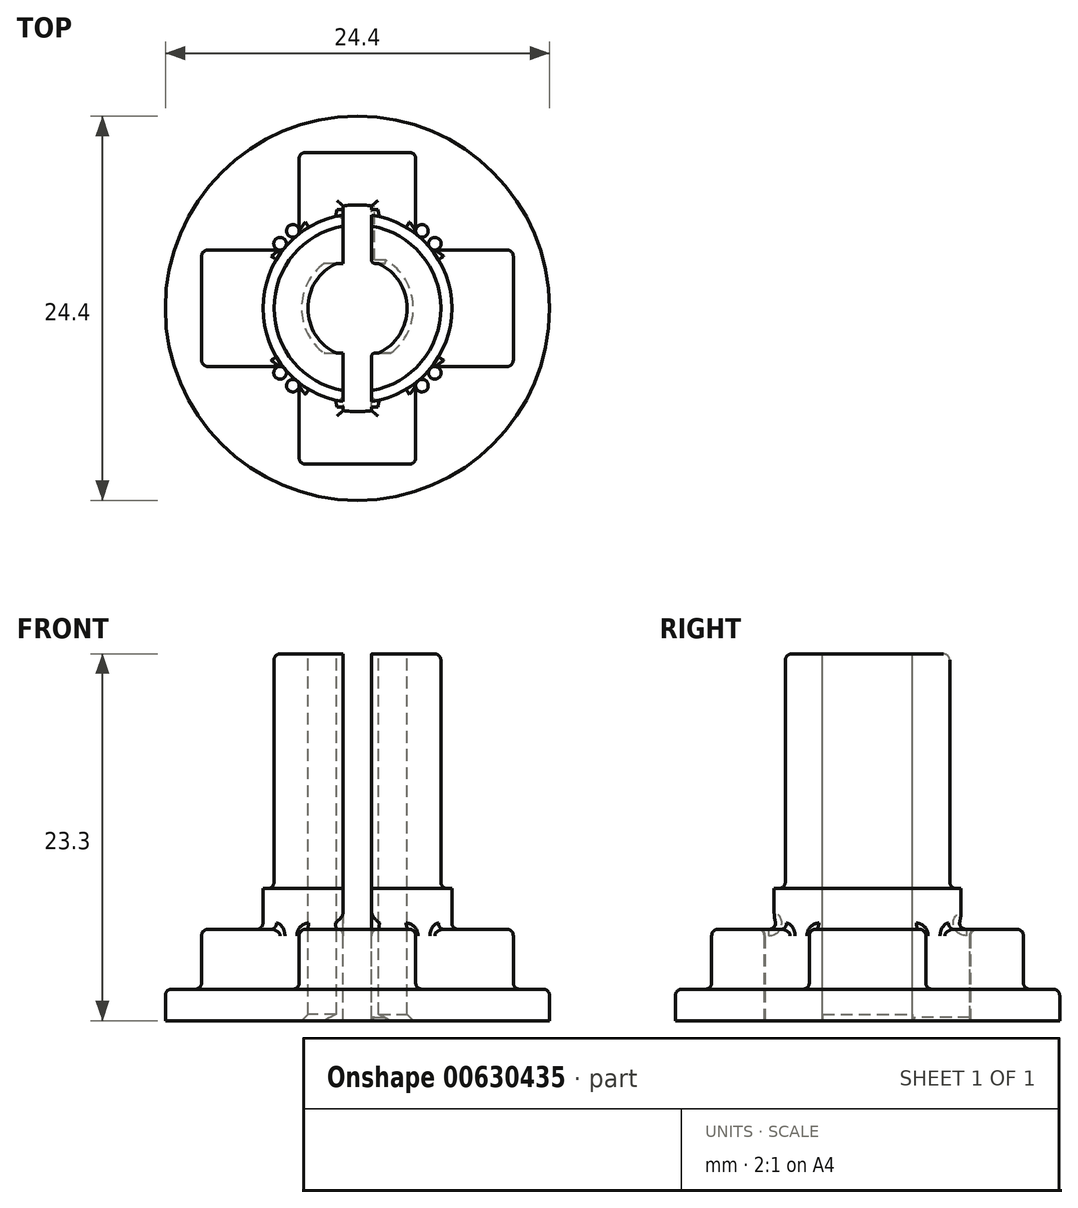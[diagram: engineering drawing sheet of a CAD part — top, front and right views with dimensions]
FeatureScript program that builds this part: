
annotation { "Feature Type Name" : "Feature", "Feature Type Description" : "" }
export const myFeature = defineFeature(function(context is Context, id is Id, definition is map)
    precondition{}
    {
        {
            var Q0;
            Q0=qCreatedBy(makeId("Front.planeOp"),FACE);
            var sketch = newSketch(context, id + "F0", { "sketchPlane" : qUnion([Q0])});
            skLineSegment(sketch, "E0", {"start": v(-12.2, 2) * mm, "end": v(-12.2, 0) * mm});
            skLineSegment(sketch, "E1", {"start": v(-12.2, 2) * mm, "end": v(-6, 2) * mm});
            skLineSegment(sketch, "E2", {"start": v(-6, 2) * mm, "end": v(-6, 8.4) * mm});
            skLineSegment(sketch, "E3", {"start": v(-6, 8.4) * mm, "end": v(-5.3, 8.4) * mm});
            skLineSegment(sketch, "E4", {"start": v(-5.3, 8.4) * mm, "end": v(-5.3, 23.3) * mm});
            skLineSegment(sketch, "E5", {"start": v(0, 23.3) * mm, "end": v(0, 0) * mm});
            skLineSegment(sketch, "E6", {"start": v(-5.3, 23.3) * mm, "end": v(-3.15, 23.3) * mm});
            skLineSegment(sketch, "E7", {"start": v(-3.15, 23.3) * mm, "end": v(-3.15, 0) * mm});
            skLineSegment(sketch, "E8", {"start": v(-12.2, 0) * mm, "end": v(-3.15, 0) * mm});
            skSolve(sketch);
        }
        {
            var Q0;
            Q0=makeQuery(id+"F0.imprint","IMPRINT",FACE,{"disambiguationData":[TD([[makeQuery(id+"F0.imprint","IMPRINT",EDGE,{"derivedFrom":sQuery(id+"F0.wireOp",EDGE,"E0")}),1.0]])]});
            var Q1;
            Q1=sQuery(id+"F0.wireOp",EDGE,"E5");
            revolve(context, id + "F1", {"entities" : qUnion([Q0]), "axis" : qUnion([Q1]), "revolveType" : RevolveType.FULL});
        }
        {
            var Q0;
            Q0=makeQuery(id+"F1.opRevolve","SWEPT_FACE",FACE,{"disambiguationData":[OSD([sQuery(id+"F0.wireOp",EDGE,"E1")])]});
            var sketch = newSketch(context, id + "F2", { "sketchPlane" : qUnion([Q0])});
            skCircle(sketch, "E9.0", {"center": v(0, 0) * mm, "radius": 6 * mm});
            skLineSegment(sketch, "E10", {"start": v(-3.7, 9.9) * mm, "end": v(3.7, 9.9) * mm});
            skLineSegment(sketch, "E11", {"start": v(3.7, 9.9) * mm, "end": v(3.7, 4.72) * mm});
            skLineSegment(sketch, "E12", {"start": v(-3.7, 9.9) * mm, "end": v(-3.7, 4.72) * mm});
            skLineSegment(sketch, "E13.1.0", {"start": v(-9.9, -3.7) * mm, "end": v(-4.72, -3.7) * mm});
            skLineSegment(sketch, "E13.1.1", {"start": v(-9.9, -3.7) * mm, "end": v(-9.9, 3.7) * mm});
            skLineSegment(sketch, "E13.1.2", {"start": v(-9.9, 3.7) * mm, "end": v(-4.72, 3.7) * mm});
            skLineSegment(sketch, "E13.2.0", {"start": v(3.7, -9.9) * mm, "end": v(3.7, -4.72) * mm});
            skLineSegment(sketch, "E13.2.1", {"start": v(3.7, -9.9) * mm, "end": v(-3.7, -9.9) * mm});
            skLineSegment(sketch, "E13.2.2", {"start": v(-3.7, -9.9) * mm, "end": v(-3.7, -4.72) * mm});
            skLineSegment(sketch, "E13.3.0", {"start": v(9.9, 3.7) * mm, "end": v(4.72, 3.7) * mm});
            skLineSegment(sketch, "E13.3.1", {"start": v(9.9, 3.7) * mm, "end": v(9.9, -3.7) * mm});
            skLineSegment(sketch, "E13.3.2", {"start": v(9.9, -3.7) * mm, "end": v(4.72, -3.7) * mm});
            skSolve(sketch);
        }
        {
            var Q0;
            {var subQ0=sQuery(id+"F2.wireOp",EDGE,"E13.1.0");Q0=makeQuery(id+"F2.imprint","IMPRINT",FACE,{"disambiguationData":[TD([[makeQuery(id+"F2.imprint","IMPRINT",EDGE,{"derivedFrom":subQ0}),1.0]])]});}
            var Q1;
            {var subQ0=sQuery(id+"F2.wireOp",EDGE,"E13.2.0");Q1=makeQuery(id+"F2.imprint","IMPRINT",FACE,{"disambiguationData":[TD([[makeQuery(id+"F2.imprint","IMPRINT",EDGE,{"derivedFrom":subQ0}),1.0]])]});}
            var Q2;
            {var subQ0=sQuery(id+"F2.wireOp",EDGE,"E13.3.0");Q2=makeQuery(id+"F2.imprint","IMPRINT",FACE,{"disambiguationData":[TD([[makeQuery(id+"F2.imprint","IMPRINT",EDGE,{"derivedFrom":subQ0}),1.0]])]});}
            var Q3;
            Q3=makeQuery(id+"F2.imprint","IMPRINT",FACE,{"disambiguationData":[TD([[makeQuery(id+"F2.imprint","IMPRINT",EDGE,{"derivedFrom":sQuery(id+"F2.wireOp",EDGE,"E10")}),-1.0]])]});
            extrude(context, id + "F3", {"entities" : qUnion([Q0, Q1, Q2, Q3]), "operationType" : NewBodyOperationType.ADD, "depth" : 3.8 * mm, "offsetDistance" : 25 * mm});
        }
        {
            var Q0;
            Q0=makeQuery(id+"F1.opRevolve","SWEPT_FACE",FACE,{"disambiguationData":[OSD([sQuery(id+"F0.wireOp",EDGE,"E6")])]});
            var sketch = newSketch(context, id + "F4", { "sketchPlane" : qUnion([Q0])});
            skCircle(sketch, "E14.0", {"center": v(0, 0) * mm, "radius": 3.15 * mm});
            skLineSegment(sketch, "E15", {"start": v(1.34, 2.85) * mm, "end": v(-1.34, 2.85) * mm});
            skLineSegment(sketch, "E16", {"start": v(1.34, -2.85) * mm, "end": v(-1.34, -2.85) * mm});
            skSolve(sketch);
        }
        {
            var Q0;
            {var subQ0=sQuery(id+"F4.wireOp",EDGE,"E15");Q0=makeQuery(id+"F4.imprint","IMPRINT",FACE,{"disambiguationData":[TD([[makeQuery(id+"F4.imprint","IMPRINT",EDGE,{"derivedFrom":subQ0}),-1.0]])]});}
            var Q1;
            {var subQ0=sQuery(id+"F4.wireOp",EDGE,"E16");Q1=makeQuery(id+"F4.imprint","IMPRINT",FACE,{"disambiguationData":[TD([[makeQuery(id+"F4.imprint","IMPRINT",EDGE,{"derivedFrom":subQ0}),1.0]])]});}
            var Q2;
            Q2=makeQuery(id+"F1.opRevolve","SWEPT_FACE",FACE,{"disambiguationData":[OSD([sQuery(id+"F0.wireOp",EDGE,"E8")])]});
            extrude(context, id + "F5", {"entities" : qUnion([Q0, Q1]), "operationType" : NewBodyOperationType.ADD, "endBound" : BoundingType.UP_TO_SURFACE, "oppositeDirection" : true, "depth" : 25 * mm, "endBoundEntityFace" : qUnion([Q2]), "offsetDistance" : 25 * mm});
        }
        {
            var Q0;
            {var subQ0=sQuery(id+"F4.wireOp",EDGE,"E14.0");Q0=makeQuery(id+"F5.boolean.opBoolean","MERGE",FACE,{"derivedFrom":[makeQuery(id+"F1.opRevolve","SWEPT_FACE",FACE,{"disambiguationData":[OSD([sQuery(id+"F0.wireOp",EDGE,"E6")])]}),makeQuery(id+"F5.opExtrude","CAP_FACE",FACE,{"disambiguationData":[OSD([subQ0,sQuery(id+"F4.wireOp",EDGE,"E15")])],"isStart":true}),makeQuery(id+"F5.opExtrude","CAP_FACE",FACE,{"disambiguationData":[OSD([subQ0,sQuery(id+"F4.wireOp",EDGE,"E16")])],"isStart":true})]});}
            var sketch = newSketch(context, id + "F6", { "sketchPlane" : qUnion([Q0])});
            skLineSegment(sketch, "E17", {"start": v(0.9, -2.85) * mm, "end": v(0.9, -6.5) * mm});
            skLineSegment(sketch, "E18", {"start": v(0.9, -6.5) * mm, "end": v(-0.9, -6.5) * mm});
            skLineSegment(sketch, "E19", {"start": v(-0.9, -6.5) * mm, "end": v(-0.9, -2.85) * mm});
            skLineSegment(sketch, "E20.1.0", {"start": v(-0.9, 2.85) * mm, "end": v(-0.9, 6.5) * mm});
            skLineSegment(sketch, "E20.1.1", {"start": v(-0.9, 6.5) * mm, "end": v(0.9, 6.5) * mm});
            skLineSegment(sketch, "E20.1.2", {"start": v(0.9, 6.5) * mm, "end": v(0.9, 2.85) * mm});
            skPoint(sketch, "E20.center", {"position": v(0, 0) * mm});
            skArc(sketch, "E21", {"start": v(0.9, 6.5) * mm, "mid": v(0, 6.56) * mm, "end": v(-0.9, 6.5) * mm});
            skArc(sketch, "E22.trimOffspring", {"start": v(-0.9, -6.5) * mm, "mid": v(0, -6.56) * mm, "end": v(0.9, -6.5) * mm});
            skSolve(sketch);
        }
        {
            var Q0;
            {var subQ0=sQuery(id+"F6.wireOp",EDGE,"E17");Q0=makeQuery(id+"F6.imprint","IMPRINT",FACE,{"disambiguationData":[TD([[makeQuery(id+"F6.imprint","IMPRINT",EDGE,{"derivedFrom":subQ0}),-1.0]])]});}
            var Q1;
            {var subQ0=sQuery(id+"F6.wireOp",EDGE,"E20.1.0");Q1=makeQuery(id+"F6.imprint","IMPRINT",FACE,{"disambiguationData":[TD([[makeQuery(id+"F6.imprint","IMPRINT",EDGE,{"derivedFrom":subQ0}),-1.0]])]});}
            var Q2;
            Q2=makeQuery(id+"F6.imprint","IMPRINT",FACE,{"disambiguationData":[TD([[makeQuery(id+"F6.imprint","IMPRINT",EDGE,{"derivedFrom":sQuery(id+"F6.wireOp",EDGE,"E18")}),1.0]])]});
            var Q3;
            Q3=makeQuery(id+"F6.imprint","IMPRINT",FACE,{"disambiguationData":[TD([[makeQuery(id+"F6.imprint","IMPRINT",EDGE,{"derivedFrom":sQuery(id+"F6.wireOp",EDGE,"E20.1.1")}),1.0]])]});
            var Q4;
            {var subQ0=sQuery(id+"F4.wireOp",EDGE,"E14.0");Q4=makeQuery(id+"F5.boolean.opBoolean","MERGE",FACE,{"derivedFrom":[makeQuery(id+"F1.opRevolve","SWEPT_FACE",FACE,{"disambiguationData":[OSD([sQuery(id+"F0.wireOp",EDGE,"E8")])]}),makeQuery(id+"F5.opExtrude","CAP_FACE",FACE,{"disambiguationData":[OSD([subQ0,sQuery(id+"F4.wireOp",EDGE,"E15")])],"isStart":false}),makeQuery(id+"F5.opExtrude","CAP_FACE",FACE,{"disambiguationData":[OSD([subQ0,sQuery(id+"F4.wireOp",EDGE,"E16")])],"isStart":false})]});}
            extrude(context, id + "F7", {"entities" : qUnion([Q0, Q1, Q2, Q3]), "operationType" : NewBodyOperationType.REMOVE, "endBound" : BoundingType.UP_TO_SURFACE, "oppositeDirection" : true, "depth" : 25 * mm, "endBoundEntityFace" : qUnion([Q4]), "offsetDistance" : 25 * mm});
        }
        {
            var Q0;
            Q0=makeQuery(id+"F1.opRevolve","SWEPT_FACE",FACE,{"disambiguationData":[OSD([sQuery(id+"F0.wireOp",EDGE,"E1")])]});
            var Q1;
            Q1=makeQuery(id+"F3.opExtrude","SWEPT_FACE",FACE,{"disambiguationData":[OSD([sQuery(id+"F2.wireOp",EDGE,"E13.3.0")])]});
            var Q2;
            Q2=makeQuery(id+"F3.opExtrude","CAP_FACE",FACE,{"disambiguationData":[OSD([sQuery(id+"F2.wireOp",EDGE,"E9.0"),sQuery(id+"F2.wireOp",EDGE,"E13.3.0"),sQuery(id+"F2.wireOp",EDGE,"E13.3.1"),sQuery(id+"F2.wireOp",EDGE,"E13.3.2")])],"isStart":false});
            var Q3;
            Q3=makeQuery(id+"F3.opExtrude","SWEPT_FACE",FACE,{"disambiguationData":[OSD([sQuery(id+"F2.wireOp",EDGE,"E13.3.2")])]});
            var Q4;
            Q4=makeQuery(id+"F3.opExtrude","SWEPT_FACE",FACE,{"disambiguationData":[OSD([sQuery(id+"F2.wireOp",EDGE,"E11")])]});
            var Q5;
            Q5=makeQuery(id+"F3.opExtrude","CAP_FACE",FACE,{"disambiguationData":[OSD([sQuery(id+"F2.wireOp",EDGE,"E9.0"),sQuery(id+"F2.wireOp",EDGE,"E10"),sQuery(id+"F2.wireOp",EDGE,"E11"),sQuery(id+"F2.wireOp",EDGE,"E12")])],"isStart":false});
            var Q6;
            Q6=makeQuery(id+"F3.opExtrude","SWEPT_FACE",FACE,{"disambiguationData":[OSD([sQuery(id+"F2.wireOp",EDGE,"E12")])]});
            var Q7;
            Q7=makeQuery(id+"F3.opExtrude","SWEPT_FACE",FACE,{"disambiguationData":[OSD([sQuery(id+"F2.wireOp",EDGE,"E13.1.2")])]});
            var Q8;
            Q8=makeQuery(id+"F3.opExtrude","CAP_FACE",FACE,{"disambiguationData":[OSD([sQuery(id+"F2.wireOp",EDGE,"E9.0"),sQuery(id+"F2.wireOp",EDGE,"E13.1.0"),sQuery(id+"F2.wireOp",EDGE,"E13.1.1"),sQuery(id+"F2.wireOp",EDGE,"E13.1.2")])],"isStart":false});
            var Q9;
            Q9=makeQuery(id+"F3.opExtrude","SWEPT_FACE",FACE,{"disambiguationData":[OSD([sQuery(id+"F2.wireOp",EDGE,"E13.1.0")])]});
            var Q10;
            Q10=makeQuery(id+"F3.opExtrude","SWEPT_FACE",FACE,{"disambiguationData":[OSD([sQuery(id+"F2.wireOp",EDGE,"E13.2.2")])]});
            var Q11;
            Q11=makeQuery(id+"F3.opExtrude","CAP_FACE",FACE,{"disambiguationData":[OSD([sQuery(id+"F2.wireOp",EDGE,"E9.0"),sQuery(id+"F2.wireOp",EDGE,"E13.2.0"),sQuery(id+"F2.wireOp",EDGE,"E13.2.1"),sQuery(id+"F2.wireOp",EDGE,"E13.2.2")])],"isStart":false});
            var Q12;
            Q12=makeQuery(id+"F3.opExtrude","SWEPT_FACE",FACE,{"disambiguationData":[OSD([sQuery(id+"F2.wireOp",EDGE,"E13.2.0")])]});
            fillet(context, id + "F8", {"entities" : qUnion([Q0, Q1, Q2, Q3, Q4, Q5, Q6, Q7, Q8, Q9, Q10, Q11, Q12]), "radius" : .4 * mm, "tangentPropagation" : true, "allowEdgeOverflow" : false});
        }
        {
            var Q0;
            Q0=makeQuery(id+"F1.opRevolve","SWEPT_EDGE",EDGE,{"disambiguationData":[OSD([sQuery(id+"F0.wireOp",EDGE,"E3"),sQuery(id+"F0.wireOp",EDGE,"E4")])]});
            var Q1;
            Q1=makeQuery(id+"F1.opRevolve","SWEPT_EDGE",EDGE,{"disambiguationData":[OSD([sQuery(id+"F0.wireOp",EDGE,"E4"),sQuery(id+"F0.wireOp",EDGE,"E6")])]});
            fillet(context, id + "F9", {"entities" : qUnion([Q0, Q1]), "radius" : .4 * mm, "tangentPropagation" : true, "allowEdgeOverflow" : false});
        }
        {
            var Q0;
            Q0=makeQuery(id+"F7.boolean.opBoolean","COPY",EDGE,{"derivedFrom":makeQuery(id+"F7.opExtrude","SWEPT_EDGE",EDGE,{"disambiguationData":[OSD([sQuery(id+"F4.wireOp",EDGE,"E15"),sQuery(id+"F6.wireOp",EDGE,"E20.1.0")])]})});
            var Q1;
            Q1=makeQuery(id+"F7.boolean.opBoolean","COPY",EDGE,{"derivedFrom":makeQuery(id+"F7.opExtrude","SWEPT_EDGE",EDGE,{"disambiguationData":[OSD([sQuery(id+"F4.wireOp",EDGE,"E15"),sQuery(id+"F6.wireOp",EDGE,"E20.1.2")])]})});
            var Q2;
            Q2=makeQuery(id+"F7.boolean.opBoolean","COPY",EDGE,{"derivedFrom":makeQuery(id+"F7.opExtrude","SWEPT_EDGE",EDGE,{"disambiguationData":[OSD([sQuery(id+"F4.wireOp",EDGE,"E16"),sQuery(id+"F6.wireOp",EDGE,"E17")])]})});
            var Q3;
            Q3=makeQuery(id+"F7.boolean.opBoolean","COPY",EDGE,{"derivedFrom":makeQuery(id+"F7.opExtrude","SWEPT_EDGE",EDGE,{"disambiguationData":[OSD([sQuery(id+"F4.wireOp",EDGE,"E16"),sQuery(id+"F6.wireOp",EDGE,"E19")])]})});
            fillet(context, id + "F10", {"entities" : qUnion([Q0, Q1, Q2, Q3]), "radius" : .2 * mm, "tangentPropagation" : true, "allowEdgeOverflow" : false});
        }
        {
            var Q0;
            Q0=makeQuery(id+"F5.boolean.opBoolean","SPLIT",EDGE,{"disambiguationData":[OD(0.0)],"derivedFrom":makeQuery(id+"F1.opRevolve","SWEPT_EDGE",EDGE,{"disambiguationData":[OSD([sQuery(id+"F0.wireOp",EDGE,"E7"),sQuery(id+"F0.wireOp",EDGE,"E8")])]})});
            var Q1;
            Q1=makeQuery(id+"F5.boolean.opBoolean","SPLIT",EDGE,{"disambiguationData":[OD(1.0)],"derivedFrom":makeQuery(id+"F1.opRevolve","SWEPT_EDGE",EDGE,{"disambiguationData":[OSD([sQuery(id+"F0.wireOp",EDGE,"E7"),sQuery(id+"F0.wireOp",EDGE,"E8")])]})});
            chamfer(context, id + "F11", {"entities" : qUnion([Q0, Q1]), "width" : .4 * mm, "tangentPropagation" : true});
        }
        {
            var Q0;
            Q0=makeQuery(id+"F7.boolean.opBoolean","COPY",EDGE,{"derivedFrom":makeQuery(id+"F7.opExtrude","CAP_EDGE",EDGE,{"disambiguationData":[OSD([sQuery(id+"F6.wireOp",EDGE,"E21")])],"isStart":false})});
            var Q1;
            Q1=makeQuery(id+"F7.boolean.opBoolean","COPY",EDGE,{"derivedFrom":makeQuery(id+"F7.opExtrude","CAP_EDGE",EDGE,{"disambiguationData":[OSD([sQuery(id+"F6.wireOp",EDGE,"E20.1.2")])],"isStart":false})});
            var Q2;
            Q2=makeQuery(id+"F7.boolean.opBoolean","COPY",EDGE,{"derivedFrom":makeQuery(id+"F7.opExtrude","CAP_EDGE",EDGE,{"disambiguationData":[OSD([sQuery(id+"F6.wireOp",EDGE,"E20.1.0")])],"isStart":false})});
            var Q3;
            {var subQ0=sQuery(id+"F4.wireOp",EDGE,"E14.0");var subQ1=sQuery(id+"F4.wireOp",EDGE,"E15");Q3=makeQuery(id+"F10.opFillet","BLEND_EDGE",EDGE,{"blendedFrom":[makeQuery(id+"F7.boolean.opBoolean","COPY",EDGE,{"derivedFrom":makeQuery(id+"F7.opExtrude","SWEPT_EDGE",EDGE,{"disambiguationData":[OSD([subQ1,sQuery(id+"F6.wireOp",EDGE,"E20.1.2")])]})}),makeQuery(id+"F5.boolean.opBoolean","MERGE",FACE,{"derivedFrom":[makeQuery(id+"F1.opRevolve","SWEPT_FACE",FACE,{"disambiguationData":[OSD([sQuery(id+"F0.wireOp",EDGE,"E8")])]}),makeQuery(id+"F5.opExtrude","CAP_FACE",FACE,{"disambiguationData":[OSD([subQ0,subQ1])],"isStart":false}),makeQuery(id+"F5.opExtrude","CAP_FACE",FACE,{"disambiguationData":[OSD([subQ0,sQuery(id+"F4.wireOp",EDGE,"E16")])],"isStart":false})]})],"blendedInto":[makeQuery(id+"F5.boolean.opBoolean","MERGE",FACE,{"derivedFrom":[makeQuery(id+"F1.opRevolve","SWEPT_FACE",FACE,{"disambiguationData":[OSD([sQuery(id+"F0.wireOp",EDGE,"E8")])]}),makeQuery(id+"F5.opExtrude","CAP_FACE",FACE,{"disambiguationData":[OSD([subQ0,subQ1])],"isStart":false}),makeQuery(id+"F5.opExtrude","CAP_FACE",FACE,{"disambiguationData":[OSD([subQ0,sQuery(id+"F4.wireOp",EDGE,"E16")])],"isStart":false})]})]});}
            var Q4;
            Q4=makeQuery(id+"F7.boolean.opBoolean","COPY",EDGE,{"derivedFrom":makeQuery(id+"F7.opExtrude","CAP_EDGE",EDGE,{"disambiguationData":[OSD([sQuery(id+"F6.wireOp",EDGE,"E17")])],"isStart":false})});
            var Q5;
            Q5=makeQuery(id+"F7.boolean.opBoolean","COPY",EDGE,{"derivedFrom":makeQuery(id+"F7.opExtrude","CAP_EDGE",EDGE,{"disambiguationData":[OSD([sQuery(id+"F6.wireOp",EDGE,"E19")])],"isStart":false})});
            var Q6;
            Q6=makeQuery(id+"F7.boolean.opBoolean","COPY",EDGE,{"derivedFrom":makeQuery(id+"F7.opExtrude","CAP_EDGE",EDGE,{"disambiguationData":[OSD([sQuery(id+"F6.wireOp",EDGE,"E22.trimOffspring")])],"isStart":false})});
            chamfer(context, id + "F12", {"entities" : qUnion([Q0, Q1, Q2, Q3, Q4, Q5, Q6]), "width" : .2 * mm, "tangentPropagation" : true});
        }
    });
